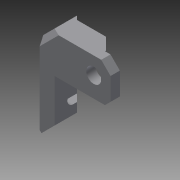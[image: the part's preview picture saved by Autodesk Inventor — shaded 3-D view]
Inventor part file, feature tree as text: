
AUTODESK INVENTOR PART (.ipt)
format: ipt  version: 2015 SP2 (Build 190223200, 223)  size: 179,200 bytes
history: native  units: mm
features: sketch x7, chamfer x6, extrude x5, hole x2
ambient origin geometry x8: Origin, YZ Plane, XZ Plane, XY Plane, X Axis, Y Axis, Z Axis, Center Point
bodies: Solid1 (feature_tree)
feature tree (20):
  extrude  "Extrusion1"  Depth=38.0mm
  extrude  "Extrusion2"  Depth=8.0mm
  extrude  "Extrusion3"  Depth=16.0mm TaperAngle=0.0deg
  extrude  "Extrusion4"  Depth=11.0mm
  chamfer  "Chamfer1"  Distance=5.0mm
  chamfer  "Chamfer2"  Distance=7.0mm
  chamfer  "Chamfer3"  Distance=15.5mm
  chamfer  "Chamfer4"  Distance=8.0mm
  chamfer  "Chamfer5"  Distance=4.0mm
  chamfer  "Chamfer6"  Distance=11.0mm
  hole  "Hole1"  [1 undecoded]
  extrude  "Extrusion5"  Depth=7.0mm TaperAngle=45.0deg
  hole  "Hole2"  [1 undecoded]
  sketch  "Sketch1"  dims[d0=38.0mm d1=50.0mm]
  sketch  "Sketch2"  dims[d2=16.0mm d3=0.0mm d4=8.0mm]
  sketch  "Sketch3"  dims[d5=20.0mm d6=16.0mm d7=0.0mm]
  sketch  "Sketch4"  dims[d8=5.0mm d9=11.0mm]
  sketch  "Sketch5"  dims[d10=0.0mm]
  sketch  "Sketch6"  dims[d11=0.5mm]
  sketch  "Sketch7"  dims[d12=8.0mm d13=5.0mm d16=7.0mm d17=15.5mm d18=8.0mm d19=4.0mm d20=11.0mm d21=0.0mm d22=7.0mm d23=7.0mm d24=45.0deg d25=6.0mm d26=6.0mm d27=45.0deg d28=1.0mm d29=1.0mm d30=45.0deg d31=5.0mm d32=5.0mm d33=45.0deg d34=3.0mm d35=3.0mm d36=45.0deg d37=2.0mm d38=3.0mm d39=45.0deg d40=6.0mm d41=20.0mm d45=10.0mm d46=3.6mm d47=6.0mm d48=6.2mm d49=4.0mm d50=90.0deg d51=8.0mm d52=20.594885mm d53=6.2mm d54=6.2mm d55=20.0mm d56=4.0mm d57=10.0mm d58=6.0mm d59=0.0mm d60=9.0mm d61=10.8mm d62=8.0mm d63=6.0mm d64=6.2mm d65=4.0mm d66=90.0deg d67=8.0mm d68=20.594885mm]
note: 2 required parameter values undecoded (feature->parameter linkage not recoverable at this tier; creation-order binding heuristic only, values carry confidence <= 0.55)
